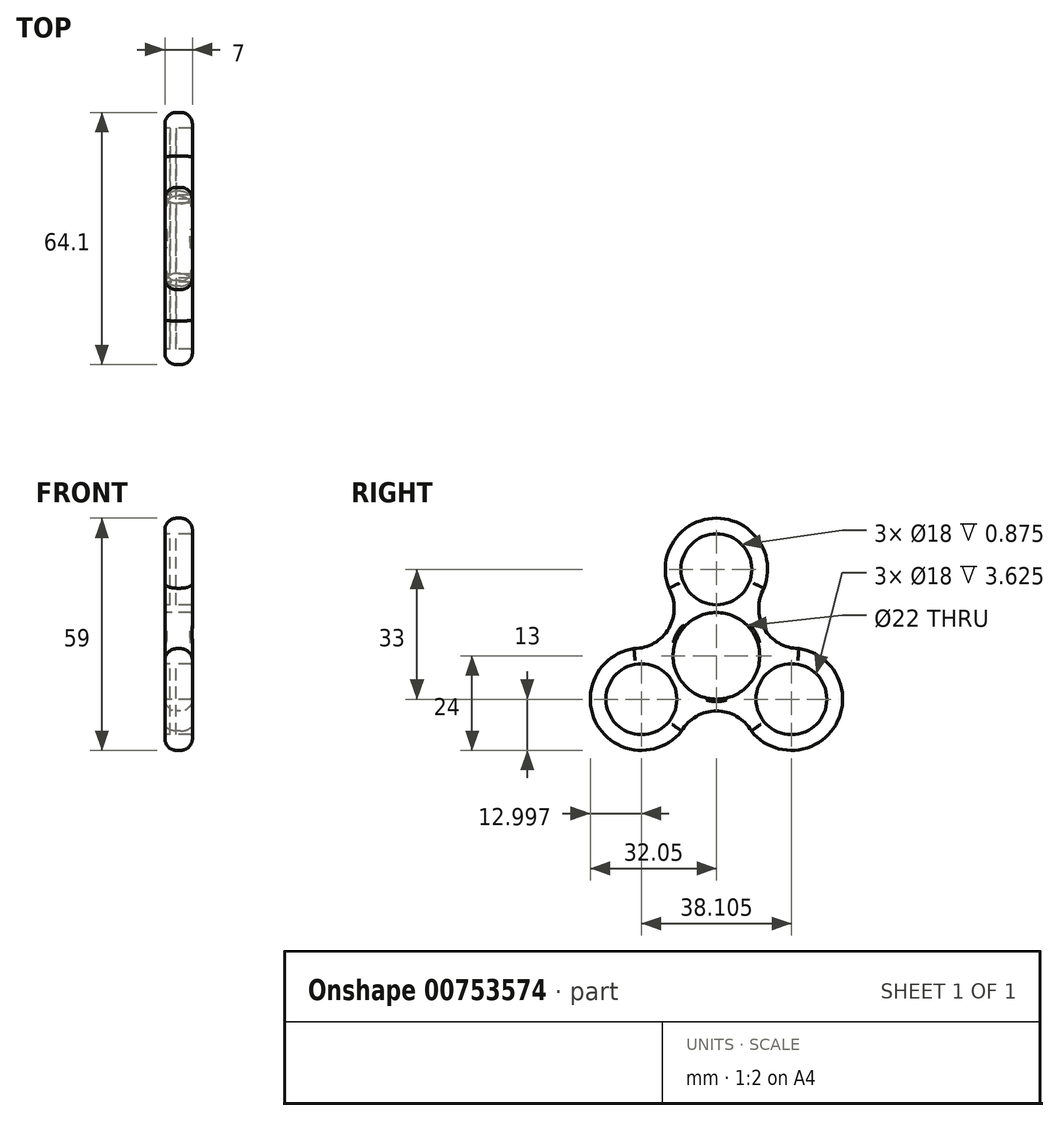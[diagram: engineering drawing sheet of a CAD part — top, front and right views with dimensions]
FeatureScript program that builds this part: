
annotation { "Feature Type Name" : "Feature", "Feature Type Description" : "" }
export const myFeature = defineFeature(function(context is Context, id is Id, definition is map)
    precondition{}
    {
        {
            var Q0;
            Q0=qCreatedBy(makeId("Right.planeOp"),FACE);
            var sketch = newSketch(context, id + "F0", { "sketchPlane" : qUnion([Q0])});
            skLineSegment(sketch, "E0", {"start": v(0, 0) * mm, "end": v(0, 22) * mm, "construction": true});
            skLineSegment(sketch, "E1", {"start": v(0, 0) * mm, "end": v(0, 35) * mm, "construction": true});
            skCircle(sketch, "E2", {"center": v(0, 22) * mm, "radius": 13 * mm});
            skCircle(sketch, "E3", {"center": v(0, 22) * mm, "radius": 9 * mm});
            skCircle(sketch, "E4.1.0", {"center": v(-19.05, -11) * mm, "radius": 9 * mm});
            skCircle(sketch, "E4.1.1", {"center": v(-19.05, -11) * mm, "radius": 13 * mm});
            skCircle(sketch, "E4.2.0", {"center": v(19.05, -11) * mm, "radius": 9 * mm});
            skCircle(sketch, "E4.2.1", {"center": v(19.05, -11) * mm, "radius": 13 * mm});
            skPoint(sketch, "E4.center", {"position": v(0, 0) * mm});
            skCircle(sketch, "E5", {"center": v(0, 0) * mm, "radius": 11 * mm});
            skLineSegment(sketch, "E6", {"start": v(0, 22) * mm, "end": v(-19.05, -11) * mm, "construction": true});
            skLineSegment(sketch, "E7", {"start": v(0, 22) * mm, "end": v(-11.26, 28.5) * mm, "construction": true});
            skLineSegment(sketch, "E8", {"start": v(-19.05, -11) * mm, "end": v(-30.31, -4.5) * mm, "construction": true});
            skLineSegment(sketch, "E9", {"start": v(-6.98, 26.03) * mm, "end": v(-24.04, -3.5) * mm, "construction": true});
            skArc(sketch, "E10", {"start": v(-20.94, 1.86) * mm, "mid": v(-12.12, 7) * mm, "end": v(-12.08, 17.2) * mm});
            skArc(sketch, "E11.1.0", {"start": v(8.86, -19.06) * mm, "mid": v(0, -14) * mm, "end": v(-8.86, -19.06) * mm});
            skArc(sketch, "E11.2.0", {"start": v(12.08, 17.2) * mm, "mid": v(12.12, 7) * mm, "end": v(20.94, 1.86) * mm});
            skSolve(sketch);
        }
        {
            var Q0;
            Q0=makeQuery(id+"F0.imprint","IMPRINT",FACE,{"disambiguationData":[TD([[makeQuery(id+"F0.imprint","IMPRINT",EDGE,{"derivedFrom":sQuery(id+"F0.wireOp",EDGE,"E4.1.0")}),-1.0]])]});
            var Q1;
            Q1=makeQuery(id+"F0.imprint","IMPRINT",FACE,{"disambiguationData":[TD([[makeQuery(id+"F0.imprint","IMPRINT",EDGE,{"derivedFrom":sQuery(id+"F0.wireOp",EDGE,"E4.2.0")}),-1.0]])]});
            var Q2;
            {var subQ0=sQuery(id+"F0.wireOp",EDGE,"81456913-f319-4308-a934-f6464afc4406.1.0");var subQ1=sQuery(id+"F0.wireOp",EDGE,"E4.1.1");var subQ2=makeQuery(id+"F0.imprint","INTERSECT",VERTEX,{"disambiguationData":[OD(1.0)],"derivedFrom":[subQ1,subQ0]});Q2=makeQuery(id+"F0.imprint","IMPRINT",FACE,{"disambiguationData":[TD([[makeQuery(id+"F0.imprint","IMPRINT",EDGE,{"disambiguationData":[TD([[subQ2,-1.0]])],"derivedFrom":subQ1}),-1.0]])]});}
            var Q3;
            {var subQ0=sQuery(id+"F0.wireOp",EDGE,"81456913-f319-4308-a934-f6464afc4406.2.0");var subQ1=sQuery(id+"F0.wireOp",EDGE,"E2");var subQ2=makeQuery(id+"F0.imprint","INTERSECT",VERTEX,{"disambiguationData":[OD(1.0)],"derivedFrom":[subQ1,subQ0]});Q3=makeQuery(id+"F0.imprint","IMPRINT",FACE,{"disambiguationData":[TD([[makeQuery(id+"F0.imprint","IMPRINT",EDGE,{"disambiguationData":[TD([[subQ2,1.0]])],"derivedFrom":subQ1}),-1.0]])]});}
            var Q4;
            {var subQ0=sQuery(id+"F0.wireOp",EDGE,"ui8VPpVe-4k2T-Ahyi-KDTx-X3uHPrizm0mL");var subQ1=sQuery(id+"F0.wireOp",EDGE,"E2");var subQ2=makeQuery(id+"F0.imprint","INTERSECT",VERTEX,{"disambiguationData":[OD(1.0)],"derivedFrom":[subQ1,subQ0]});Q4=makeQuery(id+"F0.imprint","IMPRINT",FACE,{"disambiguationData":[TD([[makeQuery(id+"F0.imprint","IMPRINT",EDGE,{"disambiguationData":[TD([[subQ2,-1.0]])],"derivedFrom":subQ1}),-1.0]])]});}
            var Q5;
            Q5=makeQuery(id+"F0.imprint","IMPRINT",FACE,{"disambiguationData":[TD([[makeQuery(id+"F0.imprint","IMPRINT",EDGE,{"derivedFrom":sQuery(id+"F0.wireOp",EDGE,"E3")}),-1.0]])]});
            var Q6;
            {var subQ0=sQuery(id+"F0.wireOp",EDGE,"ghdhOXPy-kQU6-4iIx-QLF7-a8XFwSQhsniU");var subQ1=sQuery(id+"F0.wireOp",EDGE,"E2");var subQ2=makeQuery(id+"F0.imprint","INTERSECT",VERTEX,{"disambiguationData":[OD(1.0)],"derivedFrom":[subQ1,subQ0]});Q6=makeQuery(id+"F0.imprint","IMPRINT",FACE,{"disambiguationData":[TD([[makeQuery(id+"F0.imprint","IMPRINT",EDGE,{"disambiguationData":[TD([[subQ2,-1.0]])],"derivedFrom":subQ1}),-1.0]])]});}
            var Q7;
            {var subQ0=sQuery(id+"F0.wireOp",EDGE,"dd0dd2e1-a6e1-4fd6-b5fc-92d59b18e6f1.1.0");var subQ1=sQuery(id+"F0.wireOp",EDGE,"E4.1.1");var subQ2=makeQuery(id+"F0.imprint","INTERSECT",VERTEX,{"disambiguationData":[OD(1.0)],"derivedFrom":[subQ1,subQ0]});Q7=makeQuery(id+"F0.imprint","IMPRINT",FACE,{"disambiguationData":[TD([[makeQuery(id+"F0.imprint","IMPRINT",EDGE,{"disambiguationData":[TD([[subQ2,-1.0]])],"derivedFrom":subQ1}),-1.0]])]});}
            var Q8;
            {var subQ0=sQuery(id+"F0.wireOp",EDGE,"dd0dd2e1-a6e1-4fd6-b5fc-92d59b18e6f1.2.0");var subQ1=sQuery(id+"F0.wireOp",EDGE,"E2");var subQ2=makeQuery(id+"F0.imprint","INTERSECT",VERTEX,{"disambiguationData":[OD(1.0)],"derivedFrom":[subQ1,subQ0]});Q8=makeQuery(id+"F0.imprint","IMPRINT",FACE,{"disambiguationData":[TD([[makeQuery(id+"F0.imprint","IMPRINT",EDGE,{"disambiguationData":[TD([[subQ2,1.0]])],"derivedFrom":subQ1}),-1.0]])]});}
            var Q9;
            {var subQ0=sQuery(id+"F0.wireOp",EDGE,"E10");var subQ1=sQuery(id+"F0.wireOp",EDGE,"E2");var subQ2=makeQuery(id+"F0.imprint","INTERSECT",VERTEX,{"disambiguationData":[OD(1.0)],"derivedFrom":[subQ1,subQ0]});Q9=makeQuery(id+"F0.imprint","IMPRINT",FACE,{"disambiguationData":[TD([[makeQuery(id+"F0.imprint","IMPRINT",EDGE,{"disambiguationData":[TD([[subQ2,-1.0]])],"derivedFrom":subQ1}),-1.0]])]});}
            var Q10;
            {var subQ0=sQuery(id+"F0.wireOp",EDGE,"E11.1.0");var subQ1=sQuery(id+"F0.wireOp",EDGE,"E4.1.1");var subQ2=makeQuery(id+"F0.imprint","INTERSECT",VERTEX,{"disambiguationData":[OD(1.0)],"derivedFrom":[subQ1,subQ0]});Q10=makeQuery(id+"F0.imprint","IMPRINT",FACE,{"disambiguationData":[TD([[makeQuery(id+"F0.imprint","IMPRINT",EDGE,{"disambiguationData":[TD([[subQ2,-1.0]])],"derivedFrom":subQ1}),-1.0]])]});}
            var Q11;
            {var subQ0=sQuery(id+"F0.wireOp",EDGE,"E11.2.0");var subQ1=sQuery(id+"F0.wireOp",EDGE,"E2");var subQ2=makeQuery(id+"F0.imprint","INTERSECT",VERTEX,{"disambiguationData":[OD(1.0)],"derivedFrom":[subQ1,subQ0]});Q11=makeQuery(id+"F0.imprint","IMPRINT",FACE,{"disambiguationData":[TD([[makeQuery(id+"F0.imprint","IMPRINT",EDGE,{"disambiguationData":[TD([[subQ2,1.0]])],"derivedFrom":subQ1}),-1.0]])]});}
            extrude(context, id + "F1", {"entities" : qUnion([Q0, Q1, Q2, Q3, Q4, Q5, Q6, Q7, Q8, Q9, Q10, Q11]), "depth" : 7 * mm, "offsetDistance" : 25.4 * mm});
        }
        {
            var Q0;
            Q0=makeQuery(id+"F1.opExtrude","CAP_EDGE",EDGE,{"disambiguationData":[OSD([sQuery(id+"F0.wireOp",EDGE,"E10")])],"isStart":true});
            var Q1;
            Q1=makeQuery(id+"F1.opExtrude","CAP_EDGE",EDGE,{"disambiguationData":[OSD([sQuery(id+"F0.wireOp",EDGE,"E10")])],"isStart":false});
            var Q2;
            Q2=makeQuery(id+"F1.opExtrude","CAP_EDGE",EDGE,{"disambiguationData":[OSD([sQuery(id+"F0.wireOp",EDGE,"E2")])],"isStart":false});
            var Q3;
            Q3=makeQuery(id+"F1.opExtrude","CAP_EDGE",EDGE,{"disambiguationData":[OSD([sQuery(id+"F0.wireOp",EDGE,"E11.2.0")])],"isStart":false});
            var Q4;
            Q4=makeQuery(id+"F1.opExtrude","CAP_EDGE",EDGE,{"disambiguationData":[OSD([sQuery(id+"F0.wireOp",EDGE,"E11.1.0")])],"isStart":false});
            var Q5;
            Q5=makeQuery(id+"F1.opExtrude","CAP_EDGE",EDGE,{"disambiguationData":[OSD([sQuery(id+"F0.wireOp",EDGE,"E4.1.1")])],"isStart":false});
            var Q6;
            Q6=makeQuery(id+"F1.opExtrude","CAP_EDGE",EDGE,{"disambiguationData":[OSD([sQuery(id+"F0.wireOp",EDGE,"E4.2.1")])],"isStart":false});
            var Q7;
            Q7=makeQuery(id+"F1.opExtrude","CAP_EDGE",EDGE,{"disambiguationData":[OSD([sQuery(id+"F0.wireOp",EDGE,"E11.1.0")])],"isStart":true});
            var Q8;
            Q8=makeQuery(id+"F1.opExtrude","CAP_EDGE",EDGE,{"disambiguationData":[OSD([sQuery(id+"F0.wireOp",EDGE,"E4.1.1")])],"isStart":true});
            var Q9;
            Q9=makeQuery(id+"F1.opExtrude","CAP_EDGE",EDGE,{"disambiguationData":[OSD([sQuery(id+"F0.wireOp",EDGE,"E4.2.1")])],"isStart":true});
            var Q10;
            Q10=makeQuery(id+"F1.opExtrude","CAP_EDGE",EDGE,{"disambiguationData":[OSD([sQuery(id+"F0.wireOp",EDGE,"E11.2.0")])],"isStart":true});
            var Q11;
            Q11=makeQuery(id+"F1.opExtrude","CAP_EDGE",EDGE,{"disambiguationData":[OSD([sQuery(id+"F0.wireOp",EDGE,"E2")])],"isStart":true});
            fillet(context, id + "F2", {"entities" : qUnion([Q0, Q1, Q2, Q3, Q4, Q5, Q6, Q7, Q8, Q9, Q10, Q11]), "radius" : 3 * mm, "tangentPropagation" : true, "allowEdgeOverflow" : false});
        }
        {
            var Q0;
            Q0=makeQuery(id+"F1.opExtrude","CAP_EDGE",EDGE,{"disambiguationData":[OSD([sQuery(id+"F0.wireOp",EDGE,"E5")])],"isStart":false});
            var Q1;
            Q1=makeQuery(id+"F1.opExtrude","CAP_EDGE",EDGE,{"disambiguationData":[OSD([sQuery(id+"F0.wireOp",EDGE,"E5")])],"isStart":false});
            var Q2;
            Q2=makeQuery(id+"F1.opExtrude","CAP_EDGE",EDGE,{"disambiguationData":[OSD([sQuery(id+"F0.wireOp",EDGE,"E4.1.0")])],"isStart":true});
            var Q3;
            Q3=makeQuery(id+"F2.opFillet","BLEND_EDGE",EDGE,{"blendedFrom":[makeQuery(id+"F1.opExtrude","CAP_EDGE",EDGE,{"disambiguationData":[OSD([sQuery(id+"F0.wireOp",EDGE,"dd0dd2e1-a6e1-4fd6-b5fc-92d59b18e6f1.1.0")])],"isStart":true}),makeQuery(id+"F1.opExtrude","SWEPT_FACE",FACE,{"disambiguationData":[OSD([sQuery(id+"F0.wireOp",EDGE,"E5")])]})],"blendedInto":[makeQuery(id+"F1.opExtrude","SWEPT_FACE",FACE,{"disambiguationData":[OSD([sQuery(id+"F0.wireOp",EDGE,"E5")])]})]});
            var Q4;
            Q4=makeQuery(id+"F1.opExtrude","CAP_EDGE",EDGE,{"disambiguationData":[OSD([sQuery(id+"F0.wireOp",EDGE,"E4.2.0")])],"isStart":true});
            var Q5;
            Q5=makeQuery(id+"F1.opExtrude","CAP_EDGE",EDGE,{"disambiguationData":[OSD([sQuery(id+"F0.wireOp",EDGE,"E5")])],"isStart":true});
            var Q6;
            Q6=makeQuery(id+"F1.opExtrude","CAP_EDGE",EDGE,{"disambiguationData":[OSD([sQuery(id+"F0.wireOp",EDGE,"E5")])],"isStart":true});
            var Q7;
            Q7=makeQuery(id+"F1.opExtrude","CAP_EDGE",EDGE,{"disambiguationData":[OSD([sQuery(id+"F0.wireOp",EDGE,"E5")])],"isStart":true});
            var Q8;
            Q8=makeQuery(id+"F2.opFillet","BLEND_EDGE",EDGE,{"blendedFrom":[makeQuery(id+"F1.opExtrude","CAP_EDGE",EDGE,{"disambiguationData":[OSD([sQuery(id+"F0.wireOp",EDGE,"dd0dd2e1-a6e1-4fd6-b5fc-92d59b18e6f1.2.0")])],"isStart":true}),makeQuery(id+"F1.opExtrude","SWEPT_FACE",FACE,{"disambiguationData":[OSD([sQuery(id+"F0.wireOp",EDGE,"E5")])]})],"blendedInto":[makeQuery(id+"F1.opExtrude","SWEPT_FACE",FACE,{"disambiguationData":[OSD([sQuery(id+"F0.wireOp",EDGE,"E5")])]})]});
            var Q9;
            Q9=makeQuery(id+"F2.opFillet","BLEND_EDGE",EDGE,{"blendedFrom":[makeQuery(id+"F1.opExtrude","CAP_EDGE",EDGE,{"disambiguationData":[OSD([sQuery(id+"F0.wireOp",EDGE,"ghdhOXPy-kQU6-4iIx-QLF7-a8XFwSQhsniU")])],"isStart":true}),makeQuery(id+"F1.opExtrude","SWEPT_FACE",FACE,{"disambiguationData":[OSD([sQuery(id+"F0.wireOp",EDGE,"E5")])]})],"blendedInto":[makeQuery(id+"F1.opExtrude","SWEPT_FACE",FACE,{"disambiguationData":[OSD([sQuery(id+"F0.wireOp",EDGE,"E5")])]})]});
            var Q10;
            Q10=makeQuery(id+"F1.opExtrude","CAP_EDGE",EDGE,{"disambiguationData":[OSD([sQuery(id+"F0.wireOp",EDGE,"E3")])],"isStart":true});
            var Q11;
            Q11=makeQuery(id+"F2.opFillet","BLEND_EDGE",EDGE,{"blendedFrom":[makeQuery(id+"F1.opExtrude","CAP_EDGE",EDGE,{"disambiguationData":[OSD([sQuery(id+"F0.wireOp",EDGE,"dd0dd2e1-a6e1-4fd6-b5fc-92d59b18e6f1.2.0")])],"isStart":false}),makeQuery(id+"F1.opExtrude","SWEPT_FACE",FACE,{"disambiguationData":[OSD([sQuery(id+"F0.wireOp",EDGE,"E5")])]})],"blendedInto":[makeQuery(id+"F1.opExtrude","SWEPT_FACE",FACE,{"disambiguationData":[OSD([sQuery(id+"F0.wireOp",EDGE,"E5")])]})]});
            var Q12;
            Q12=makeQuery(id+"F2.opFillet","BLEND_EDGE",EDGE,{"blendedFrom":[makeQuery(id+"F1.opExtrude","CAP_EDGE",EDGE,{"disambiguationData":[OSD([sQuery(id+"F0.wireOp",EDGE,"ghdhOXPy-kQU6-4iIx-QLF7-a8XFwSQhsniU")])],"isStart":false}),makeQuery(id+"F1.opExtrude","SWEPT_FACE",FACE,{"disambiguationData":[OSD([sQuery(id+"F0.wireOp",EDGE,"E5")])]})],"blendedInto":[makeQuery(id+"F1.opExtrude","SWEPT_FACE",FACE,{"disambiguationData":[OSD([sQuery(id+"F0.wireOp",EDGE,"E5")])]})]});
            var Q13;
            Q13=makeQuery(id+"F2.opFillet","BLEND_EDGE",EDGE,{"blendedFrom":[makeQuery(id+"F1.opExtrude","CAP_EDGE",EDGE,{"disambiguationData":[OSD([sQuery(id+"F0.wireOp",EDGE,"dd0dd2e1-a6e1-4fd6-b5fc-92d59b18e6f1.1.0")])],"isStart":false}),makeQuery(id+"F1.opExtrude","SWEPT_FACE",FACE,{"disambiguationData":[OSD([sQuery(id+"F0.wireOp",EDGE,"E5")])]})],"blendedInto":[makeQuery(id+"F1.opExtrude","SWEPT_FACE",FACE,{"disambiguationData":[OSD([sQuery(id+"F0.wireOp",EDGE,"E5")])]})]});
            var Q14;
            Q14=makeQuery(id+"F1.opExtrude","CAP_EDGE",EDGE,{"disambiguationData":[OSD([sQuery(id+"F0.wireOp",EDGE,"E4.2.0")])],"isStart":false});
            var Q15;
            Q15=makeQuery(id+"F1.opExtrude","CAP_EDGE",EDGE,{"disambiguationData":[OSD([sQuery(id+"F0.wireOp",EDGE,"E4.1.0")])],"isStart":false});
            var Q16;
            Q16=makeQuery(id+"F1.opExtrude","CAP_EDGE",EDGE,{"disambiguationData":[OSD([sQuery(id+"F0.wireOp",EDGE,"E3")])],"isStart":false});
            fillet(context, id + "F3", {"entities" : qUnion([Q0, Q1, Q2, Q3, Q4, Q5, Q6, Q7, Q8, Q9, Q10, Q11, Q12, Q13, Q14, Q15, Q16]), "radius" : .5 * mm, "tangentPropagation" : true, "allowEdgeOverflow" : false});
        }
        {
            var Q0;
            Q0=qCreatedBy(makeId("Right.planeOp"),FACE);
            cPlane(context, id + "F4", {"entities" : qUnion([Q0]), "cplaneType" : CPlaneType.OFFSET, "offset" : 2.88 * mm, "width" : 152.4 * mm, "height" : 152.4 * mm});
        }
        {
            var Q0;
            Q0=qCreatedBy(id+"F4.planeOp",FACE);
            var sketch = newSketch(context, id + "F5", { "sketchPlane" : qUnion([Q0])});
            skCircle(sketch, "E12", {"center": v(-19.05, -11) * mm, "radius": 9 * mm});
            skCircle(sketch, "E13.1.0", {"center": v(19.05, -11) * mm, "radius": 9 * mm});
            skCircle(sketch, "E13.2.0", {"center": v(0, 22) * mm, "radius": 9 * mm});
            skPoint(sketch, "E13.center", {"position": v(0, 0) * mm});
            skSolve(sketch);
        }
        {
            var Q0;
            Q0 = qSketchRegion(id + "F5", true);
            extrude(context, id + "F6", {"entities" : qUnion([Q0]), "operationType" : NewBodyOperationType.ADD, "depth" : -1.5 * mm, "offsetDistance" : 25.4 * mm});
        }
    });
